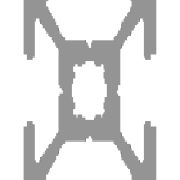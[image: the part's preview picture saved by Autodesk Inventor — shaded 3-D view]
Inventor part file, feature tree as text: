
AUTODESK INVENTOR PART (.ipt)
format: ipt  version: 2021.3 (Build 253353000, 353)  size: 287,232 bytes
history: native  units: mm
features: other x4, sketch x3, extrude x1, plane x1
ambient origin geometry x8: Origin, YZ Plane, XZ Plane, XY Plane, X Axis, Y Axis, Z Axis, Center Point
bodies: Body (feature_tree)
feature tree (9):
  other  "Driven Length"
  other  "Frame Generator"
  extrude  "Extrusion_20x20"  Depth=1.5mm
  other  "Start Plane"
  other  "End Plane"
  sketch  "Sketch"  dims[d7=3.0mm d9=1.5mm d10=0.5mm d13=0.5mm d14=0.5mm d18=3.0mm d19=3.0mm d21=0.5mm d22=0.5mm d23=0.5mm d24=2.75mm d25=1.5mm d26=10.0mm d27=10.0mm d28=3.0mm d29=3.0mm d30=5.5mm d31=1.5mm d32=0.5mm d33=0.5mm d34=0.5mm d35=0.5mm d36=0.5mm d37=0.5mm d38=0.5mm d39=0.5mm d40=0.5mm d41=2.75mm d42=2.75mm d43=0.5mm d44=40.0mm d46=360.0deg d50=-0.0mm d51=660.0mm d52=0.13mm d53=0.0mm d54=90.0deg d55=660.0mm]
  sketch  "Sketch2"  dims[d4=5.5mm d5=1.5mm]
  plane  "Work Plane3"
  sketch  "Sketch3"  dims[d6=1.5mm]
